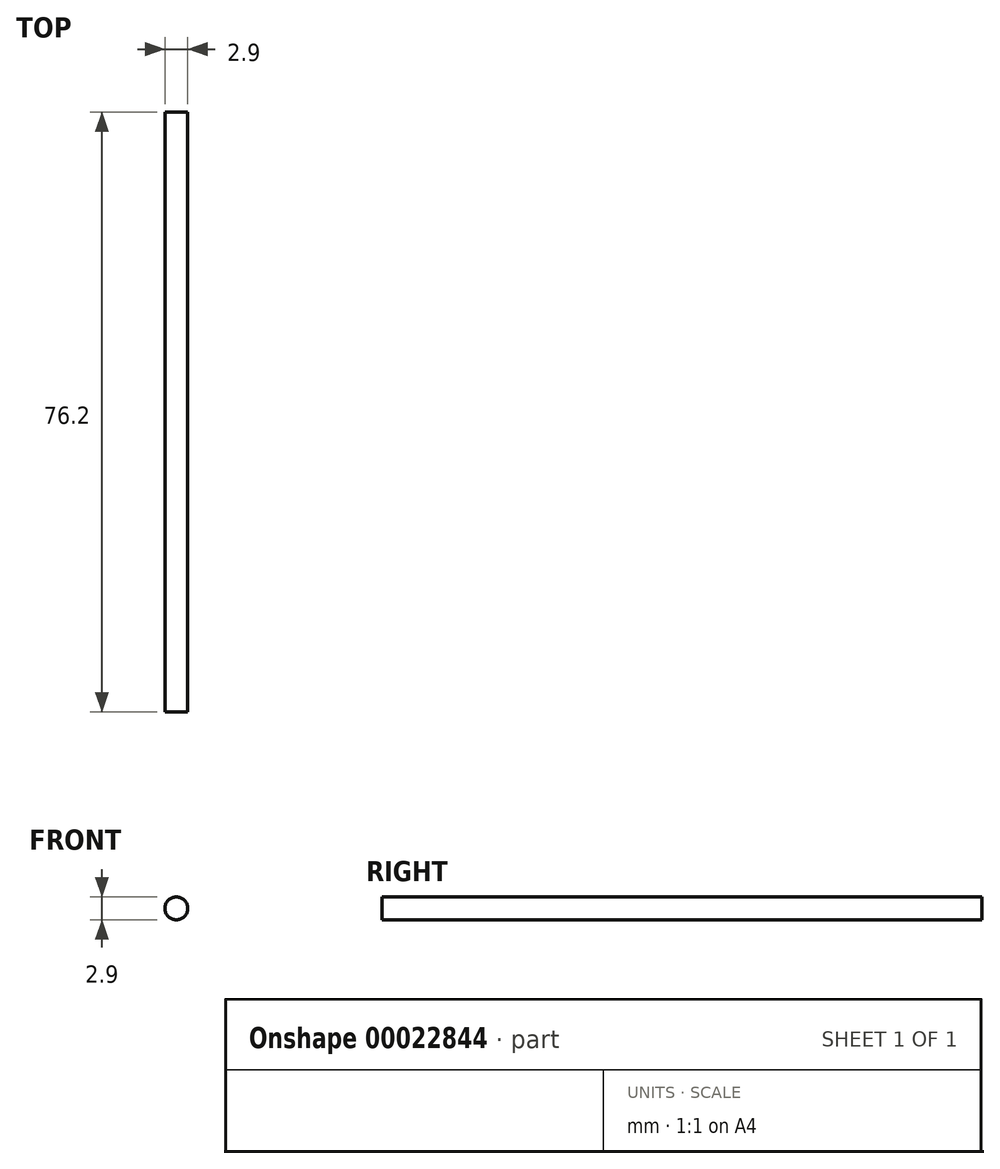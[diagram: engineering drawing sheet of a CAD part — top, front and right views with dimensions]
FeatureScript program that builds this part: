
annotation { "Feature Type Name" : "Feature", "Feature Type Description" : "" }
export const myFeature = defineFeature(function(context is Context, id is Id, definition is map)
    precondition{}
    {
        {
            var Q0;
            Q0=qCreatedBy(makeId("Front.planeOp"),FACE);
            var sketch = newSketch(context, id + "F0", { "sketchPlane" : qUnion([Q0])});
            skCircle(sketch, "E0", {"center": v(-86.12, 26.67) * mm, "radius": 1.45 * mm});
            skSolve(sketch);
        }
        {
            var Q0;
            Q0=makeQuery(id+"F0.imprint","IMPRINT",FACE,{"disambiguationData":[TD([[makeQuery(id+"F0.imprint","IMPRINT",EDGE,{"derivedFrom":sQuery(id+"F0.wireOp",EDGE,"E0")}),1.0]])]});
            extrude(context, id + "F1", {"entities" : qUnion([Q0]), "depth" : 76.2 * mm});
        }
    });
